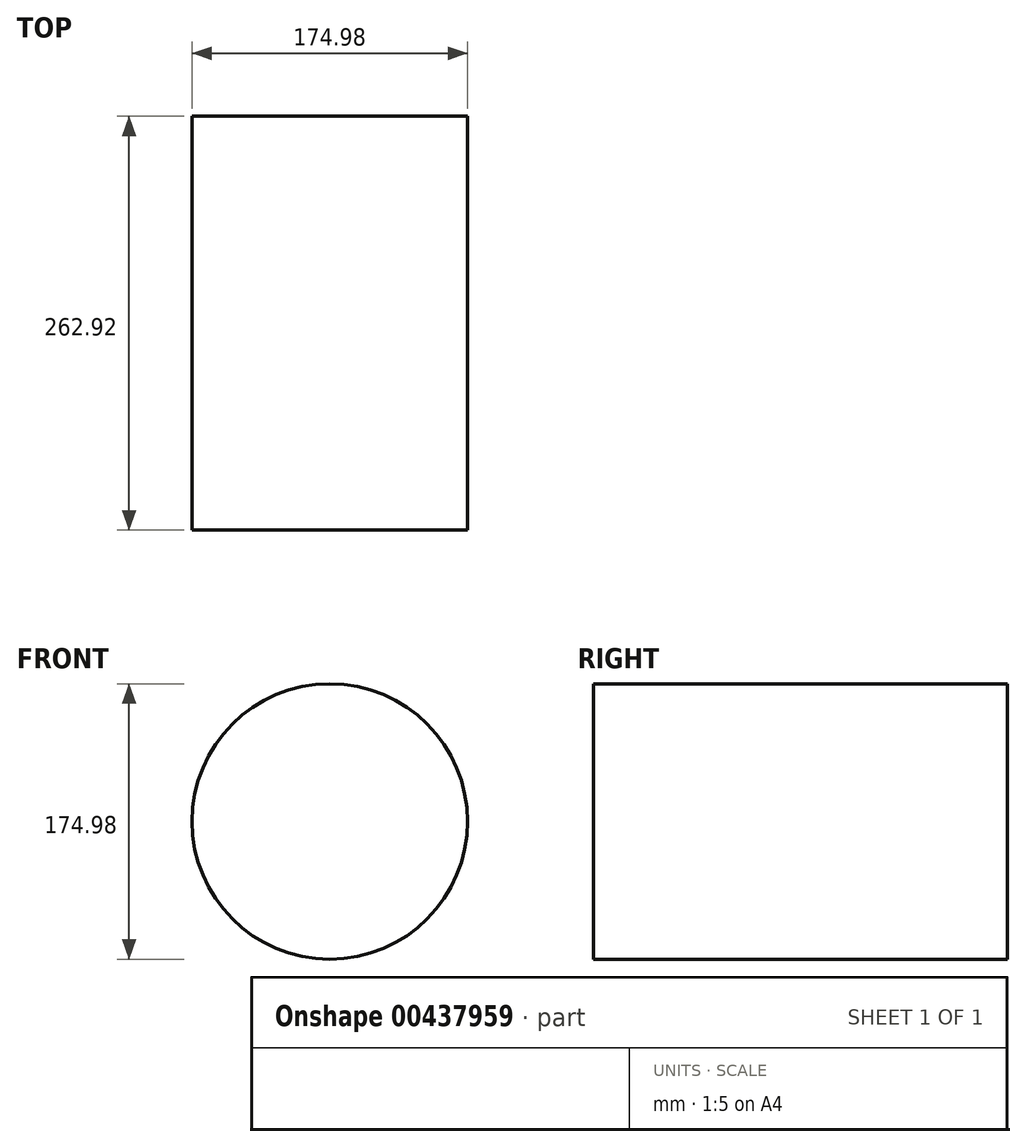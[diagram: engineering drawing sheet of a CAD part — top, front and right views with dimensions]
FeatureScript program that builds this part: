
annotation { "Feature Type Name" : "Feature", "Feature Type Description" : "" }
export const myFeature = defineFeature(function(context is Context, id is Id, definition is map)
    precondition{}
    {
        {
            var Q0;
            Q0=qCreatedBy(makeId("Front.planeOp"),FACE);
            var sketch = newSketch(context, id + "F0", { "sketchPlane" : qUnion([Q0])});
            skCircle(sketch, "E0", {"center": v(0, 0) * mm, "radius": 87.49 * mm});
            skSolve(sketch);
        }
        {
            var Q0;
            Q0=makeQuery(id+"F0.imprint","IMPRINT",FACE,{"disambiguationData":[TD([[makeQuery(id+"F0.imprint","IMPRINT",EDGE,{"derivedFrom":sQuery(id+"F0.wireOp",EDGE,"E0")}),1.0]])]});
            extrude(context, id + "F1", {"entities" : qUnion([Q0]), "depth" : 262.92 * mm});
        }
    });
